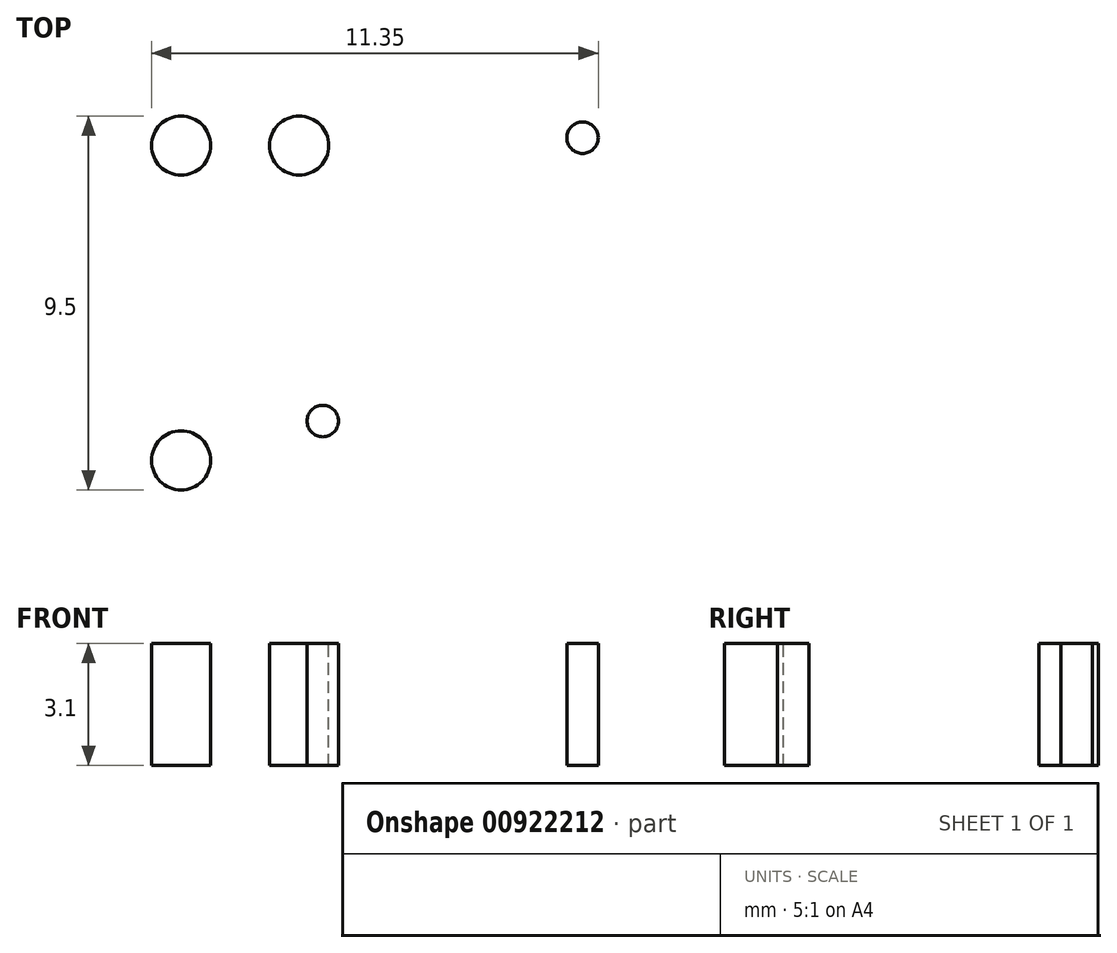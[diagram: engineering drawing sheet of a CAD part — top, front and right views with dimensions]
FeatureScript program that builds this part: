
annotation { "Feature Type Name" : "Feature", "Feature Type Description" : "" }
export const myFeature = defineFeature(function(context is Context, id is Id, definition is map)
    precondition{}
    {
        {
            var Q0;
            Q0=qCreatedBy(makeId("Top.planeOp"),FACE);
            var sketch = newSketch(context, id + "F0", { "sketchPlane" : qUnion([Q0])});
            skCircle(sketch, "E0", {"center": v(-3.24, -2.96) * mm, "radius": 0.75 * mm});
            skCircle(sketch, "E1", {"center": v(-3.24, 5.04) * mm, "radius": 0.75 * mm});
            skCircle(sketch, "E2", {"center": v(-0.24, -2.96) * mm, "radius": 0.75 * mm});
            skCircle(sketch, "E3", {"center": v(0.36, 4.04) * mm, "radius": 0.4 * mm});
            skCircle(sketch, "E4", {"center": v(6.96, -3.16) * mm, "radius": 0.4 * mm});
            skSolve(sketch);
        }
        {
            var Q0;
            Q0 = qSketchRegion(id + "F0", true);
            extrude(context, id + "F1", {"entities" : qUnion([Q0]), "depth" : 3.1 * mm, "offsetDistance" : 25 * mm});
        }
        {
            var Q0;
            Q0=qCreatedBy(makeId("Front.planeOp"),FACE);
            var sketch = newSketch(context, id + "F2", { "sketchPlane" : qUnion([Q0])});
            skLineSegment(sketch, "E5", {"start": v(0, 0) * mm, "end": v(-7.6, 0) * mm});
            skSolve(sketch);
        }
        {
            var Q0;
            Q0=makeQuery(id+"F1.opExtrude","SWEPT_BODY",BODY,{"disambiguationData":[OSD([sQuery(id+"F0.wireOp",EDGE,"E2")])]});
            var Q1;
            Q1=makeQuery(id+"F1.opExtrude","SWEPT_BODY",BODY,{"disambiguationData":[OSD([sQuery(id+"F0.wireOp",EDGE,"E0")])]});
            var Q2;
            Q2=makeQuery(id+"F1.opExtrude","SWEPT_BODY",BODY,{"disambiguationData":[OSD([sQuery(id+"F0.wireOp",EDGE,"E4")])]});
            var Q3;
            Q3=makeQuery(id+"F1.opExtrude","SWEPT_BODY",BODY,{"disambiguationData":[OSD([sQuery(id+"F0.wireOp",EDGE,"E3")])]});
            var Q4;
            Q4=makeQuery(id+"F1.opExtrude","SWEPT_BODY",BODY,{"disambiguationData":[OSD([sQuery(id+"F0.wireOp",EDGE,"E1")])]});
            var Q5;
            Q5=sQuery(id+"F2.wireOp",EDGE,"E5");
            transform(context, id + "F3", {"entities" : qUnion([Q0, Q1, Q2, Q3, Q4]), "transformType" : TransformType.ROTATION, "transformAxis" : qUnion([Q5]), "angle" : 180 * degree, "makeCopy" : false});
        }
    });
